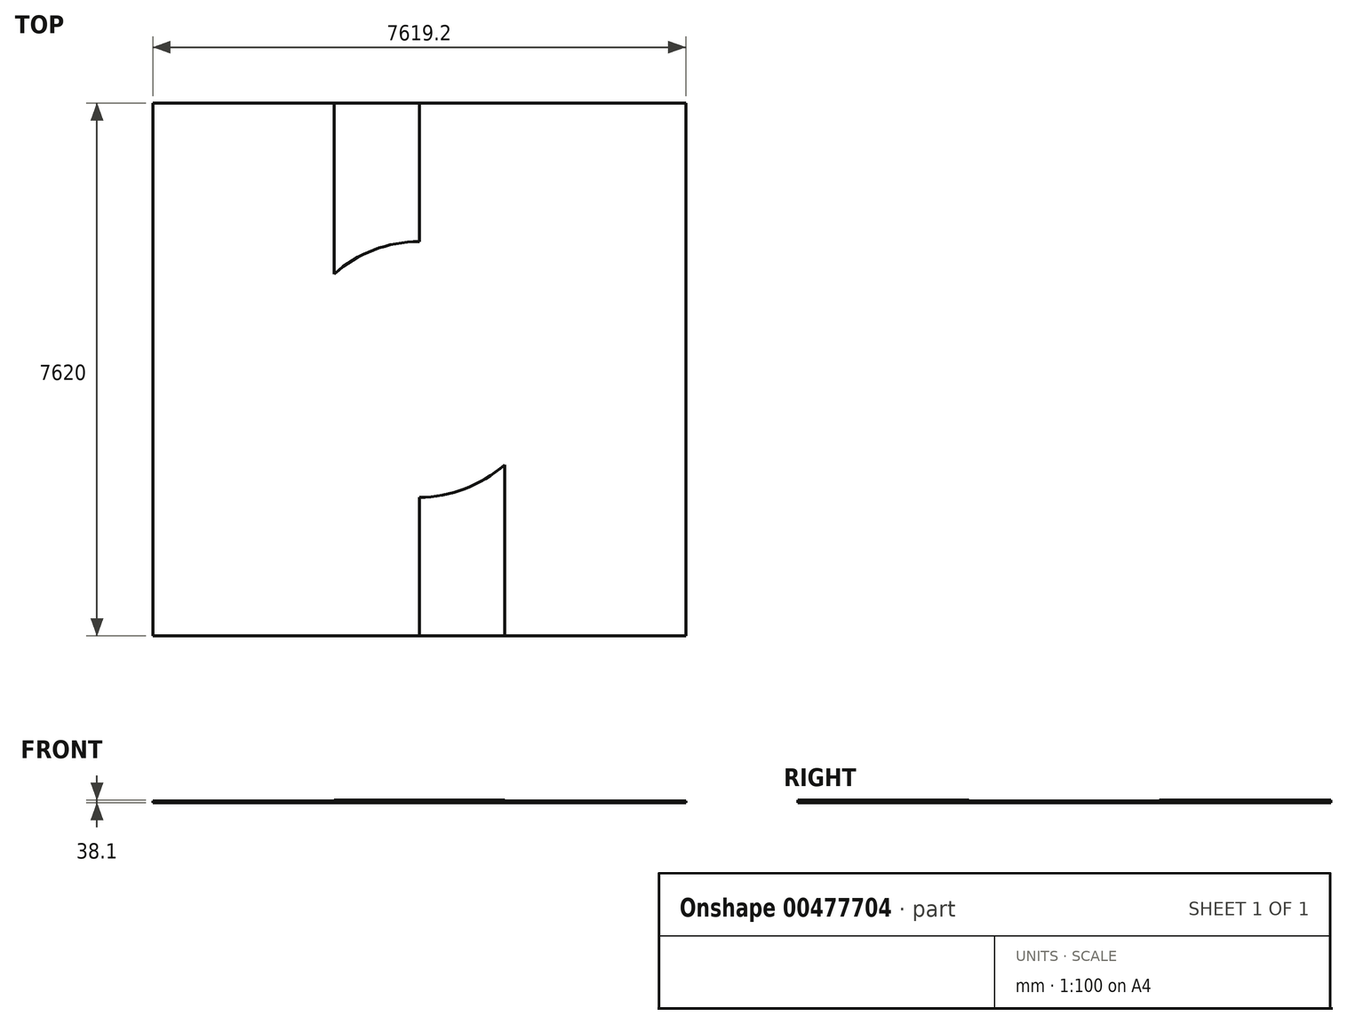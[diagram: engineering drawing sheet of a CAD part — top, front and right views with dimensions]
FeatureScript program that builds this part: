
annotation { "Feature Type Name" : "Feature", "Feature Type Description" : "" }
export const myFeature = defineFeature(function(context is Context, id is Id, definition is map)
    precondition{}
    {
        {
            var Q0;
            Q0=qCreatedBy(makeId("Top.planeOp"),FACE);
            var sketch = newSketch(context, id + "F0", { "sketchPlane" : qUnion([Q0])});
            skLineSegment(sketch, "E0.bottom", {"start": v(-3809.6, 3810) * mm, "end": v(3809.6, 3810) * mm});
            skLineSegment(sketch, "E0.top", {"start": v(-3809.6, -3810) * mm, "end": v(3809.6, -3810) * mm});
            skLineSegment(sketch, "E0.left", {"start": v(-3809.6, 3810) * mm, "end": v(-3809.6, -3810) * mm});
            skLineSegment(sketch, "E0.right", {"start": v(3809.6, 3810) * mm, "end": v(3809.6, -3810) * mm});
            skCircle(sketch, "E1", {"center": v(0, 0) * mm, "radius": 1828.8 * mm});
            skLineSegment(sketch, "E2", {"start": v(1219.2, -1363.1) * mm, "end": v(1219.2, -3810) * mm});
            skLineSegment(sketch, "E3", {"start": v(0, -2339.34) * mm, "end": v(1219.2, -2339.34) * mm});
            skPoint(sketch, "E3.endSnap0", {"position": v(1219.2, -2586.55) * mm});
            skLineSegment(sketch, "E4", {"start": v(0, -3116.58) * mm, "end": v(1219.2, -3116.58) * mm});
            skLineSegment(sketch, "E5", {"start": v(-1219.2, 1363.1) * mm, "end": v(-1219.2, 3810) * mm});
            skLineSegment(sketch, "E6", {"start": v(-1219.2, 2247.9) * mm, "end": v(0, 2247.9) * mm});
            skLineSegment(sketch, "E7", {"start": v(-1219.2, 3040.38) * mm, "end": v(0, 3040.38) * mm});
            skCircle(sketch, "E8", {"center": v(0, 0) * mm, "radius": 1790.7 * mm});
            skLineSegment(sketch, "E9", {"start": v(0, -3116.58) * mm, "end": v(0, -3810) * mm});
            skLineSegment(sketch, "E10", {"start": v(0, -2339.34) * mm, "end": v(0, -1828.8) * mm});
            skLineSegment(sketch, "E11", {"start": v(0, -3116.58) * mm, "end": v(0, -2339.34) * mm});
            skLineSegment(sketch, "E12", {"start": v(0, 2247.9) * mm, "end": v(0, 1828.8) * mm});
            skLineSegment(sketch, "E13", {"start": v(0, 2247.9) * mm, "end": v(0, 3040.38) * mm});
            skLineSegment(sketch, "E14", {"start": v(0, 3040.38) * mm, "end": v(0, 3810) * mm});
            skSolve(sketch);
        }
        {
            var Q0;
            {var subQ5=sQuery(id+"F0.wireOp",EDGE,"E0.left");Q0=makeQuery(id+"F0.imprint","IMPRINT",FACE,{"disambiguationData":[TD([[makeQuery(id+"F0.imprint","IMPRINT",EDGE,{"derivedFrom":subQ5}),1.0]])]});}
            var Q1;
            {var subQ8=sQuery(id+"F0.wireOp",EDGE,"E0.right");Q1=makeQuery(id+"F0.imprint","IMPRINT",FACE,{"disambiguationData":[TD([[makeQuery(id+"F0.imprint","IMPRINT",EDGE,{"derivedFrom":subQ8}),-1.0]])]});}
            var Q2;
            {var subQ0=sQuery(id+"F0.wireOp",EDGE,"E1");var subQ1=makeQuery(id+"F0.imprint","INTERSECT",VERTEX,{"derivedFrom":[subQ0,sQuery(id+"F0.wireOp",EDGE,"E5")]});Q2=makeQuery(id+"F0.imprint","IMPRINT",FACE,{"disambiguationData":[TD([[makeQuery(id+"F0.imprint","IMPRINT",EDGE,{"disambiguationData":[TD([[subQ1,1.0]])],"derivedFrom":subQ0}),1.0]])]});}
            var Q3;
            {var subQ1=sQuery(id+"F0.wireOp",EDGE,"E1");var subQ8=makeQuery(id+"F0.imprint","INTERSECT",VERTEX,{"derivedFrom":[subQ1,sQuery(id+"F0.wireOp",EDGE,"E2")]});Q3=makeQuery(id+"F0.imprint","IMPRINT",FACE,{"disambiguationData":[TD([[makeQuery(id+"F0.imprint","IMPRINT",EDGE,{"disambiguationData":[TD([[subQ8,1.0]])],"derivedFrom":subQ1}),1.0]])]});}
            extrude(context, id + "F1", {"entities" : qUnion([Q0, Q1, Q2, Q3]), "depth" : 25.4 * mm});
        }
        {
            var Q0;
            Q0=sQuery(id+"F0.wireOp",EDGE,"E1");
            extrude(context, id + "F2", {"bodyType" : ToolBodyType.SURFACE, "surfaceEntities" : qUnion([Q0]), "depth" : 50.8 * mm});
        }
        {
            var Q0;
            Q0 = qSketchRegion(id + "F0", true);
            extrude(context, id + "F3", {"entities" : qUnion([Q0]), "operationType" : NewBodyOperationType.ADD, "depth" : 25.4 * mm});
        }
        {
            var Q0;
            Q0=makeQuery(id+"F0.imprint","IMPRINT",FACE,{"disambiguationData":[TD([[makeQuery(id+"F0.imprint","IMPRINT",EDGE,{"derivedFrom":sQuery(id+"F0.wireOp",EDGE,"E8")}),1.0]])]});
            extrude(context, id + "F4", {"entities" : qUnion([Q0]), "operationType" : NewBodyOperationType.ADD, "depth" : 25.4 * mm});
        }
        {
            var Q0;
            {var subQ4=sQuery(id+"F0.wireOp",EDGE,"E7");Q0=makeQuery(id+"F0.imprint","IMPRINT",FACE,{"disambiguationData":[TD([[makeQuery(id+"F0.imprint","IMPRINT",EDGE,{"derivedFrom":subQ4}),1.0]])]});}
            var Q1;
            {var subQ4=sQuery(id+"F0.wireOp",EDGE,"E6");Q1=makeQuery(id+"F0.imprint","IMPRINT",FACE,{"disambiguationData":[TD([[makeQuery(id+"F0.imprint","IMPRINT",EDGE,{"derivedFrom":subQ4}),-1.0]])]});}
            var Q2;
            {var subQ0=sQuery(id+"F0.wireOp",EDGE,"E6");Q2=makeQuery(id+"F0.imprint","IMPRINT",FACE,{"disambiguationData":[TD([[makeQuery(id+"F0.imprint","IMPRINT",EDGE,{"derivedFrom":subQ0}),1.0]])]});}
            var Q3;
            {var subQ4=sQuery(id+"F0.wireOp",EDGE,"E3");Q3=makeQuery(id+"F0.imprint","IMPRINT",FACE,{"disambiguationData":[TD([[makeQuery(id+"F0.imprint","IMPRINT",EDGE,{"derivedFrom":subQ4}),1.0]])]});}
            var Q4;
            {var subQ0=sQuery(id+"F0.wireOp",EDGE,"E3");Q4=makeQuery(id+"F0.imprint","IMPRINT",FACE,{"disambiguationData":[TD([[makeQuery(id+"F0.imprint","IMPRINT",EDGE,{"derivedFrom":subQ0}),-1.0]])]});}
            var Q5;
            {var subQ4=sQuery(id+"F0.wireOp",EDGE,"E4");Q5=makeQuery(id+"F0.imprint","IMPRINT",FACE,{"disambiguationData":[TD([[makeQuery(id+"F0.imprint","IMPRINT",EDGE,{"derivedFrom":subQ4}),-1.0]])]});}
            extrude(context, id + "F5", {"entities" : qUnion([Q0, Q1, Q2, Q3, Q4, Q5]), "operationType" : NewBodyOperationType.ADD, "depth" : 38.1 * mm});
        }
    });
